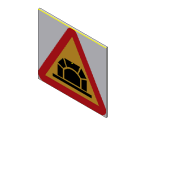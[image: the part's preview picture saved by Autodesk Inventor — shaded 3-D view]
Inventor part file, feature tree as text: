
AUTODESK INVENTOR PART (.ipt)
format: ipt  version: 2018 (Build 220112000, 112)  size: 106,496 bytes
history: native  units: in
note: dims shown in document units (in); Inventor stores cm internally (conversion verified against a paired STEP export)
features: sketch x2, extrude x1, other x1
ambient origin geometry x8: Origin, YZ Plane, XZ Plane, XY Plane, X Axis, Y Axis, Z Axis, Center Point
bodies: Body1 (feature_tree)
feature tree (4):
  extrude  "Extrusion2"  Depth=3.1496in
  sketch  "Sketch5"  dims[d43=2.7953in]
  sketch  "Sketch4"  dims[d35=0.0787in d36=0.0in d40=3.1496in]
  other  "Image5"
